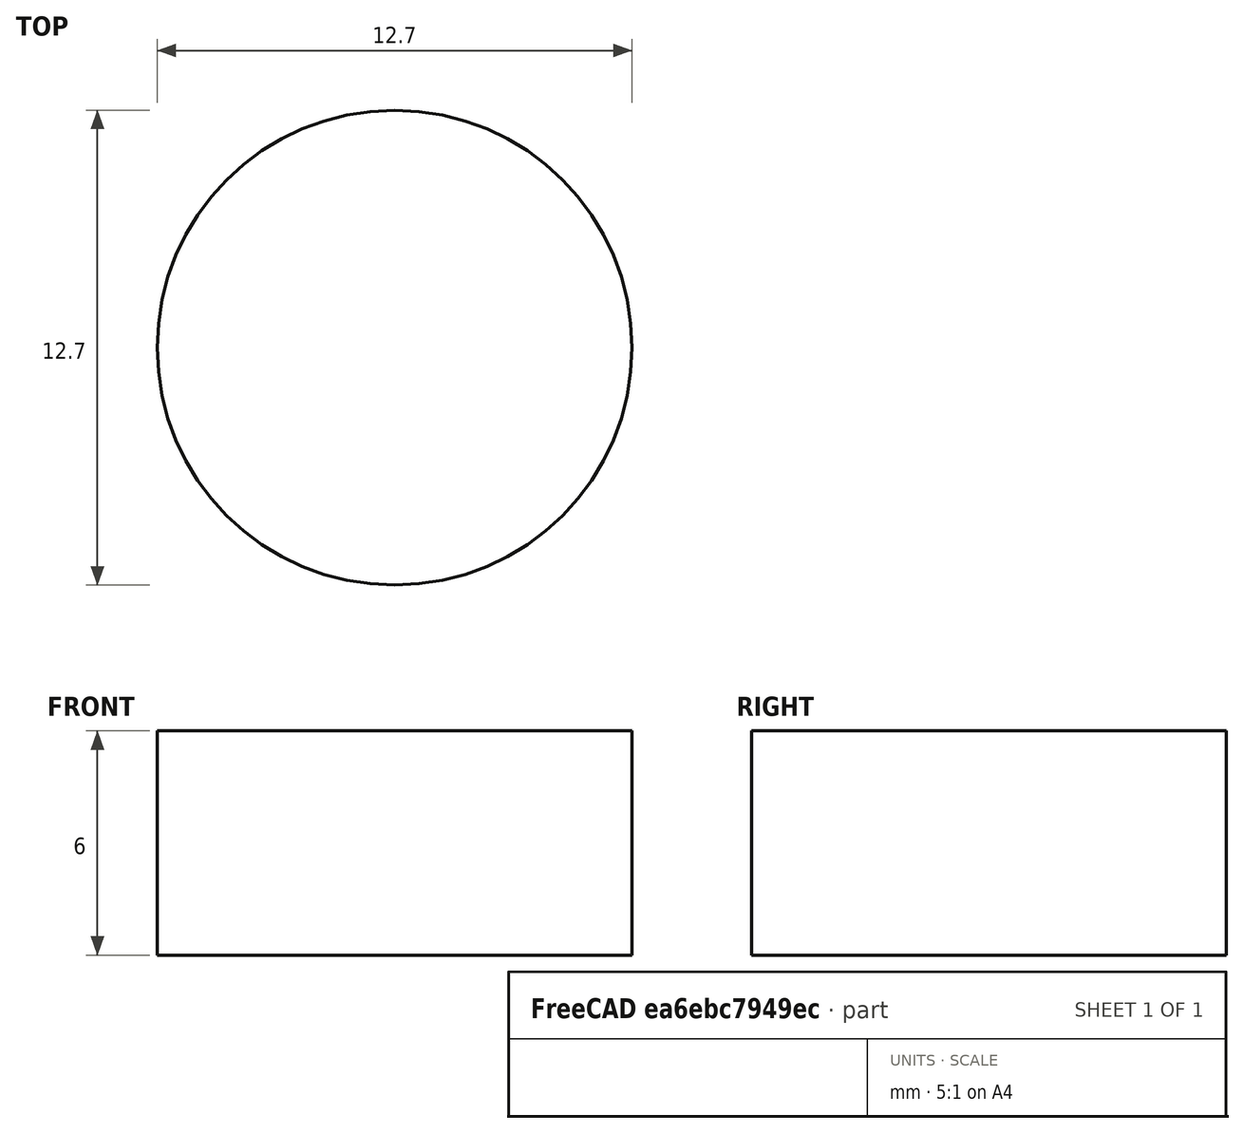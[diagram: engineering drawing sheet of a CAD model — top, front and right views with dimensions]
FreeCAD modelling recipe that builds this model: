
FCSTD DOCUMENT  (FreeCAD 0.21R33771 (Git))
Label: BB05
License: All rights reserved
LicenseURL: https://en.wikipedia.org/wiki/All_rights_reserved
objects: PartDesign::CoordinateSystem×2, Sketcher::SketchObject×1, PartDesign::Pad×1, PartDesign::Body×1, App::Part×1, Part::FeaturePython×1
note: 7 computed .brp shape members not serialized (recipe doc carries the construction recipe); baked Part::Feature solids carry a one-line shape summary decoded from their .brp

FEATURE [Sketcher::SketchObject] Sketch
  FullyConstrained = true
  MapMode = 5
  Support = -> [XY_Plane001]
  expr: Constraints[1] = 25.4 * 0.5
  sketch-geometry (1):
    g0: Circle CenterX=0 CenterY=0 CenterZ=0 NormalX=0 NormalY=0 NormalZ=1 AngleXU=0 Radius=6.35
  constraints (2):
    c: Coincident(g0,g-1)
    c: Diameter(g0) = 12.7
FEATURE [PartDesign::Pad] Pad
  Direction = (0,0,1)
  Length = 6
  Length2 = 10
  Midplane = true
  Profile = -> Sketch
  ReferenceAxis = -> Sketch [N_Axis]
  Type = 0
FEATURE [PartDesign::CoordinateSystem] LCS_Mount
  AttacherType = Attacher::AttachEngine3D
  MapMode = 11
  Placement = pos=(0,0,-3) rot=(0,0,1;1.5708rad)
  Support = -> [Pad]
FEATURE [PartDesign::CoordinateSystem] LCS_opticalCenter
  AttacherType = Attacher::AttachEngine3D
  MapMode = 11
  Placement = pos=(0,0,-3) rot=(0.707107,-0.707107,0;3.14159rad)
  Support = -> [Pad]
FEATURE [PartDesign::Body] Body  label="mirror"
  Group = -> [Sketch,Pad,LCS_Mount,LCS_opticalCenter]
  Origin = -> Origin001
  Tip = -> Pad
FEATURE [App::Part] BB05
  Group = -> [Body]
  Origin = -> Origin
FEATURE [Part::FeaturePython] Mirror  # WARN: FeaturePython — macro-defined, semantics opaque (R4)
  Base = -> [Body]
  OpticalType = 0
